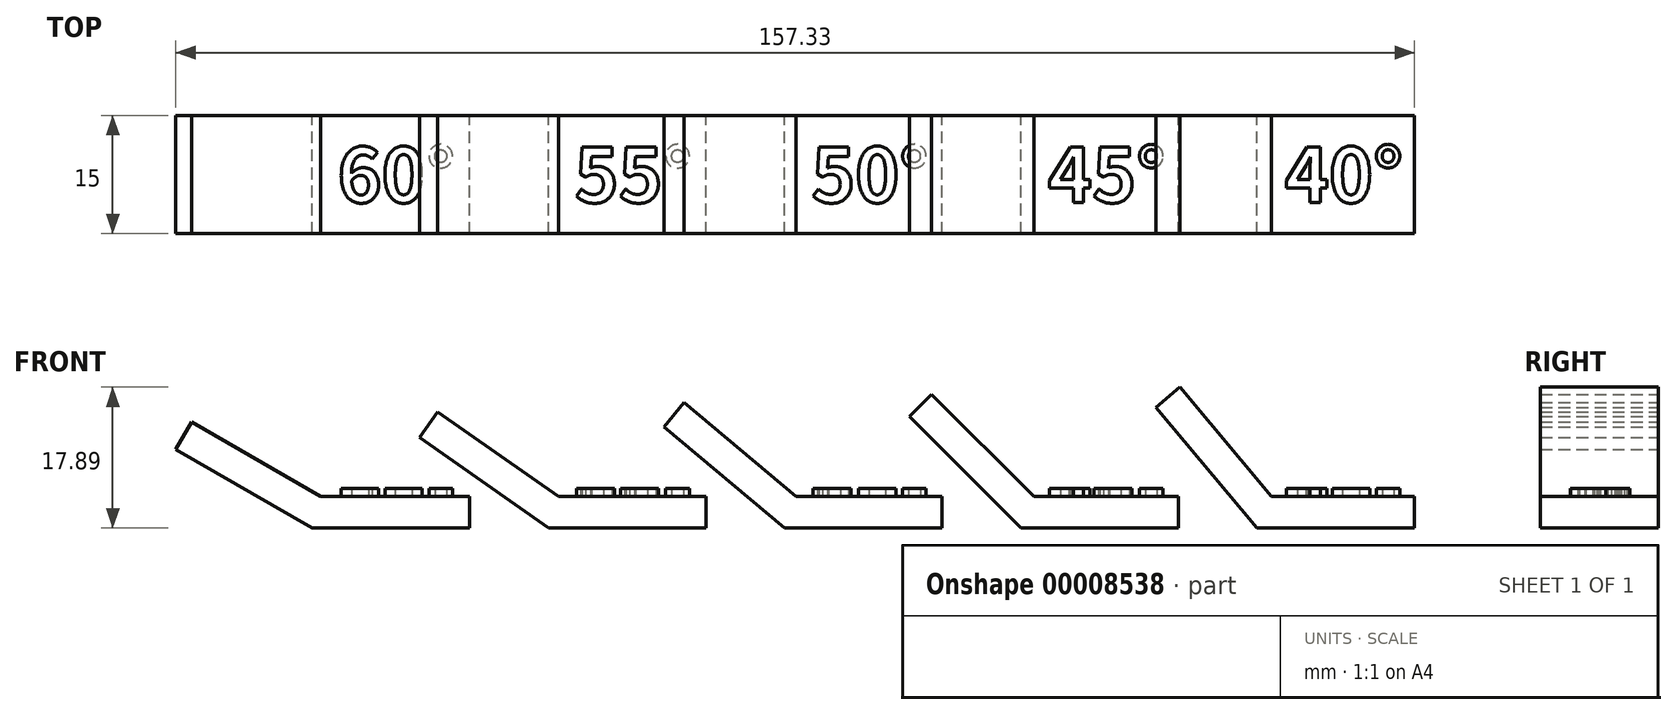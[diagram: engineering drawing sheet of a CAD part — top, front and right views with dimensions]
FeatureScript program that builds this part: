
annotation { "Feature Type Name" : "Feature", "Feature Type Description" : "" }
export const myFeature = defineFeature(function(context is Context, id is Id, definition is map)
    precondition{}
    {
        {
            var Q0;
            Q0=qCreatedBy(makeId("Front.planeOp"),FACE);
            var sketch = newSketch(context, id + "F0", { "sketchPlane" : qUnion([Q0])});
            skLineSegment(sketch, "E0", {"start": v(-89.73, -36.48) * mm, "end": v(90.27, -36.48) * mm, "construction": true});
            skLineSegment(sketch, "E1", {"start": v(-83.6, -16.92) * mm, "end": v(-49.73, -36.48) * mm, "construction": true});
            skLineSegment(sketch, "E2", {"start": v(-51.79, -14.04) * mm, "end": v(-19.73, -36.48) * mm, "construction": true});
            skLineSegment(sketch, "E3", {"start": v(-16.18, -14.3) * mm, "end": v(10.27, -36.48) * mm, "construction": true});
            skLineSegment(sketch, "E4", {"start": v(15.38, -11.6) * mm, "end": v(40.27, -36.48) * mm, "construction": true});
            skLineSegment(sketch, "E5", {"start": v(44.7, -6) * mm, "end": v(70.27, -36.48) * mm, "construction": true});
            skLineSegment(sketch, "E6", {"start": v(90.27, -36.48) * mm, "end": v(90.27, 45.04) * mm, "construction": true});
            skLineSegment(sketch, "E7", {"start": v(-29.73, -36.48) * mm, "end": v(-49.73, -36.48) * mm});
            skLineSegment(sketch, "E8", {"start": v(-49.73, -36.48) * mm, "end": v(-67.06, -26.5) * mm});
            skLineSegment(sketch, "E9", {"start": v(0.27, -36.48) * mm, "end": v(-19.73, -36.48) * mm});
            skLineSegment(sketch, "E10", {"start": v(-19.73, -36.48) * mm, "end": v(-36.11, -25.01) * mm});
            skLineSegment(sketch, "E11", {"start": v(30.27, -36.48) * mm, "end": v(10.27, -36.48) * mm});
            skLineSegment(sketch, "E12", {"start": v(10.27, -36.48) * mm, "end": v(-5.05, -23.63) * mm});
            skLineSegment(sketch, "E13", {"start": v(60.27, -36.48) * mm, "end": v(40.27, -36.48) * mm});
            skLineSegment(sketch, "E14", {"start": v(26.13, -22.34) * mm, "end": v(40.27, -36.48) * mm});
            skLineSegment(sketch, "E15", {"start": v(90.27, -36.48) * mm, "end": v(70.27, -36.48) * mm});
            skLineSegment(sketch, "E16", {"start": v(57.41, -21.16) * mm, "end": v(70.27, -36.48) * mm});
            skLineSegment(sketch, "E17.0", {"start": v(-48.66, -32.48) * mm, "end": v(-65.06, -23.03) * mm});
            skLineSegment(sketch, "E17.1", {"start": v(-29.73, -32.48) * mm, "end": v(-48.66, -32.48) * mm});
            skLineSegment(sketch, "E18.0", {"start": v(-18.47, -32.48) * mm, "end": v(-33.82, -21.74) * mm});
            skLineSegment(sketch, "E18.1", {"start": v(0.27, -32.48) * mm, "end": v(-18.47, -32.48) * mm});
            skLineSegment(sketch, "E19.0", {"start": v(11.73, -32.48) * mm, "end": v(-2.48, -20.56) * mm});
            skLineSegment(sketch, "E19.1", {"start": v(30.27, -32.48) * mm, "end": v(11.73, -32.48) * mm});
            skLineSegment(sketch, "E20.0", {"start": v(60.27, -32.48) * mm, "end": v(41.93, -32.48) * mm});
            skLineSegment(sketch, "E20.1", {"start": v(28.96, -19.51) * mm, "end": v(41.93, -32.48) * mm});
            skLineSegment(sketch, "E21.0", {"start": v(90.27, -32.48) * mm, "end": v(72.14, -32.48) * mm});
            skLineSegment(sketch, "E21.1", {"start": v(60.48, -18.6) * mm, "end": v(72.14, -32.48) * mm});
            skLineSegment(sketch, "E22", {"start": v(-65.06, -23.03) * mm, "end": v(-67.06, -26.5) * mm});
            skLineSegment(sketch, "E23", {"start": v(-29.73, -32.48) * mm, "end": v(-29.73, -36.48) * mm});
            skLineSegment(sketch, "E24", {"start": v(-36.11, -25.01) * mm, "end": v(-33.82, -21.74) * mm});
            skLineSegment(sketch, "E25", {"start": v(0.27, -36.48) * mm, "end": v(0.27, -32.48) * mm});
            skLineSegment(sketch, "E26", {"start": v(-5.05, -23.63) * mm, "end": v(-2.48, -20.56) * mm});
            skLineSegment(sketch, "E27", {"start": v(30.27, -32.48) * mm, "end": v(30.27, -36.48) * mm});
            skLineSegment(sketch, "E28", {"start": v(26.13, -22.34) * mm, "end": v(28.96, -19.51) * mm});
            skLineSegment(sketch, "E29", {"start": v(60.27, -32.48) * mm, "end": v(60.27, -36.48) * mm});
            skLineSegment(sketch, "E30", {"start": v(57.41, -21.16) * mm, "end": v(60.48, -18.6) * mm});
            skLineSegment(sketch, "E31", {"start": v(90.27, -36.48) * mm, "end": v(90.27, -32.48) * mm});
            skSolve(sketch);
        }
        {
            var Q0;
            Q0 = qSketchRegion(id + "F0", true);
            extrude(context, id + "F1", {"entities" : qUnion([Q0]), "depth" : 15 * mm});
        }
        {
            var Q0;
            Q0=makeQuery(id+"F1.opExtrude","SWEPT_FACE",FACE,{"disambiguationData":[OSD([sQuery(id+"F0.wireOp",EDGE,"E21.0")])]});
            var sketch = newSketch(context, id + "F2", { "sketchPlane" : qUnion([Q0])});
            skLineSegment(sketch, "E32.0.0", {"start": v(-29.73, 0) * mm, "end": v(-48.66, 0) * mm});
            skLineSegment(sketch, "E32.0.1", {"start": v(-48.66, 0) * mm, "end": v(-48.66, -15) * mm});
            skLineSegment(sketch, "E32.0.2", {"start": v(-48.66, -15) * mm, "end": v(-29.73, -15) * mm});
            skLineSegment(sketch, "E32.0.3", {"start": v(-29.73, -15) * mm, "end": v(-29.73, 0) * mm});
            skLineSegment(sketch, "E33.0.0", {"start": v(0.27, 0) * mm, "end": v(-18.47, 0) * mm});
            skLineSegment(sketch, "E33.0.1", {"start": v(-18.47, 0) * mm, "end": v(-18.47, -15) * mm});
            skLineSegment(sketch, "E33.0.2", {"start": v(-18.47, -15) * mm, "end": v(0.27, -15) * mm});
            skLineSegment(sketch, "E33.0.3", {"start": v(0.27, -15) * mm, "end": v(0.27, 0) * mm});
            skLineSegment(sketch, "E34.0.0", {"start": v(30.27, 0) * mm, "end": v(11.73, 0) * mm});
            skLineSegment(sketch, "E34.0.1", {"start": v(11.73, 0) * mm, "end": v(11.73, -15) * mm});
            skLineSegment(sketch, "E34.0.2", {"start": v(11.73, -15) * mm, "end": v(30.27, -15) * mm});
            skLineSegment(sketch, "E34.0.3", {"start": v(30.27, -15) * mm, "end": v(30.27, 0) * mm});
            skLineSegment(sketch, "E35.0.0", {"start": v(60.27, 0) * mm, "end": v(41.93, 0) * mm});
            skLineSegment(sketch, "E35.0.1", {"start": v(41.93, 0) * mm, "end": v(41.93, -15) * mm});
            skLineSegment(sketch, "E35.0.2", {"start": v(41.93, -15) * mm, "end": v(60.27, -15) * mm});
            skLineSegment(sketch, "E35.0.3", {"start": v(60.27, -15) * mm, "end": v(60.27, 0) * mm});
            skLineSegment(sketch, "E36.0.0", {"start": v(90.27, 0) * mm, "end": v(72.14, 0) * mm});
            skLineSegment(sketch, "E36.0.1", {"start": v(72.14, 0) * mm, "end": v(72.14, -15) * mm});
            skLineSegment(sketch, "E36.0.2", {"start": v(72.14, -15) * mm, "end": v(90.27, -15) * mm});
            skLineSegment(sketch, "E36.0.3", {"start": v(90.27, -15) * mm, "end": v(90.27, 0) * mm});
            skText(sketch, "E37", { "text": " 60°       55°       50°       45°       40°  ", "fontName": "NotoSansCJKsc-Bold.otf"});
            const initialGuessF2  = {"E37": [-0.04866, -0.01103, 1, 0, 0.00683]};
            skSetInitialGuess(sketch, initialGuessF2);
            skSolve(sketch);
        }
        {
            var Q0;
            Q0=makeQuery(id+"F2.imprint","IMPRINT",FACE,{"disambiguationData":[TD([[makeQuery(id+"F2.imprint","IMPRINT",EDGE,{"derivedFrom":sQuery(id+"F2.wireOp",EDGE,"E37.sketch_text.stroke-163")}),1.0]])]});
            var Q1;
            Q1=makeQuery(id+"F2.imprint","IMPRINT",FACE,{"disambiguationData":[TD([[makeQuery(id+"F2.imprint","IMPRINT",EDGE,{"derivedFrom":sQuery(id+"F2.wireOp",EDGE,"E37.sketch_text.stroke-155")}),1.0]])]});
            var Q2;
            Q2=makeQuery(id+"F2.imprint","IMPRINT",FACE,{"disambiguationData":[TD([[makeQuery(id+"F2.imprint","IMPRINT",EDGE,{"derivedFrom":sQuery(id+"F2.wireOp",EDGE,"E37.sketch_text.stroke-138")}),1.0]])]});
            var Q3;
            Q3=makeQuery(id+"F2.imprint","IMPRINT",FACE,{"disambiguationData":[TD([[makeQuery(id+"F2.imprint","IMPRINT",EDGE,{"derivedFrom":sQuery(id+"F2.wireOp",EDGE,"E37.sketch_text.stroke-130")}),1.0]])]});
            var Q4;
            Q4=makeQuery(id+"F2.imprint","IMPRINT",FACE,{"disambiguationData":[TD([[makeQuery(id+"F2.imprint","IMPRINT",EDGE,{"derivedFrom":sQuery(id+"F2.wireOp",EDGE,"E37.sketch_text.stroke-115")}),1.0]])]});
            var Q5;
            Q5=makeQuery(id+"F2.imprint","IMPRINT",FACE,{"disambiguationData":[TD([[makeQuery(id+"F2.imprint","IMPRINT",EDGE,{"derivedFrom":sQuery(id+"F2.wireOp",EDGE,"E37.sketch_text.stroke-98")}),1.0]])]});
            var Q6;
            Q6=makeQuery(id+"F2.imprint","IMPRINT",FACE,{"disambiguationData":[TD([[makeQuery(id+"F2.imprint","IMPRINT",EDGE,{"derivedFrom":sQuery(id+"F2.wireOp",EDGE,"E37.sketch_text.stroke-90")}),1.0]])]});
            var Q7;
            Q7=makeQuery(id+"F2.imprint","IMPRINT",FACE,{"disambiguationData":[TD([[makeQuery(id+"F2.imprint","IMPRINT",EDGE,{"derivedFrom":sQuery(id+"F2.wireOp",EDGE,"E37.sketch_text.stroke-82")}),1.0]])]});
            var Q8;
            Q8=makeQuery(id+"F2.imprint","IMPRINT",FACE,{"disambiguationData":[TD([[makeQuery(id+"F2.imprint","IMPRINT",EDGE,{"derivedFrom":sQuery(id+"F2.wireOp",EDGE,"E37.sketch_text.stroke-67")}),1.0]])]});
            var Q9;
            Q9=makeQuery(id+"F2.imprint","IMPRINT",FACE,{"disambiguationData":[TD([[makeQuery(id+"F2.imprint","IMPRINT",EDGE,{"derivedFrom":sQuery(id+"F2.wireOp",EDGE,"E37.sketch_text.stroke-59")}),1.0]])]});
            var Q10;
            Q10=makeQuery(id+"F2.imprint","IMPRINT",FACE,{"disambiguationData":[TD([[makeQuery(id+"F2.imprint","IMPRINT",EDGE,{"derivedFrom":sQuery(id+"F2.wireOp",EDGE,"E37.sketch_text.stroke-44")}),1.0]])]});
            var Q11;
            Q11=makeQuery(id+"F2.imprint","IMPRINT",FACE,{"disambiguationData":[TD([[makeQuery(id+"F2.imprint","IMPRINT",EDGE,{"derivedFrom":sQuery(id+"F2.wireOp",EDGE,"E37.sketch_text.stroke-29")}),1.0]])]});
            var Q12;
            Q12=makeQuery(id+"F2.imprint","IMPRINT",FACE,{"disambiguationData":[TD([[makeQuery(id+"F2.imprint","IMPRINT",EDGE,{"derivedFrom":sQuery(id+"F2.wireOp",EDGE,"E37.sketch_text.stroke-21")}),1.0]])]});
            var Q13;
            Q13=makeQuery(id+"F2.imprint","IMPRINT",FACE,{"disambiguationData":[TD([[makeQuery(id+"F2.imprint","IMPRINT",EDGE,{"derivedFrom":sQuery(id+"F2.wireOp",EDGE,"E37.sketch_text.stroke-13")}),1.0]])]});
            var Q14;
            Q14=makeQuery(id+"F2.imprint","IMPRINT",FACE,{"disambiguationData":[TD([[makeQuery(id+"F2.imprint","IMPRINT",EDGE,{"derivedFrom":sQuery(id+"F2.wireOp",EDGE,"E37.sketch_text.stroke-0")}),1.0]])]});
            extrude(context, id + "F3", {"entities" : qUnion([Q0, Q1, Q2, Q3, Q4, Q5, Q6, Q7, Q8, Q9, Q10, Q11, Q12, Q13, Q14]), "operationType" : NewBodyOperationType.ADD, "depth" : 1 * mm});
        }
    });
